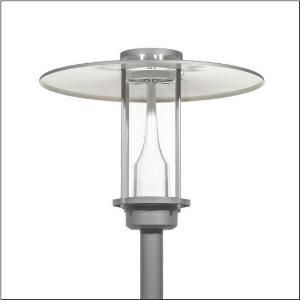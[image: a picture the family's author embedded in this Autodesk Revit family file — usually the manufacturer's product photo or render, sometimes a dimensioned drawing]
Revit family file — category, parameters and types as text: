
# Revit family: city-light_plus_iq___st1_2a_5xa5275ef14h000022_292e
name_source: partatom
category: Lighting Fixtures
units: mm (PartAtom-declared; Revit-internal decimal feet)

## family parameters
Cut with Voids When Loaded = No
Host = Face
Light Source = No
Part Type = Normal
Room Calculation Point = No
Round Connector Dimension = Use Diameter
Shared = No

## types (1)
- --- (1 x LED, 1470 lm, 10.5 W, 3000K)
    Apparent Load = 11 VA
    CIE Flux Codes = 22 62 93 97 100
    Color Rendering = 70
    Color Temperature = 3000K
    Default Elevation = 1800 mm
    Description = City-Light Plus iQ, mast luminaire, Module 540 iQ-SR, primary light control with 3 zone facetted reflector, of plastic, silver coated, highly specular, structured, primary optical cover: cover, of PMMA, transparent, light distribution: ST1.2a, light emission: direct distribution, primary light characteristic: asymmetric, installation type: post-top, LED, High Power LED, rated luminous flux: 1.470lm, luminous efficacy: 140lm/W, light colour: 730, colour temperature: 3000K, control gear: iQ Street-Remote, control: Street-Remote, Auto-Match, Temp-Guard, Lumen-Switch, Night-Set, Smart-Wire, Light-Fading, Desk-Remote (wireless, voltage-free reading and setting of iQ features in the workshop via application-optimized NFC function/RFID function), optimised constant luminous flux control (CLO 2.0), pre-setting: logarithmic dimming characteristic, mains connection: 230..240V, AC, 50/60Hz, connection cable pre-assembled, cable length: 5,5m, wiring characteristics: H07RN-F, start of lifetime: 11W, end of service life: 11W, reduction: 5W, luminaire housing, upper part, of glass-fibre reinforced polyester, coated, SITECO metallic grey (DB 702S), diameter: 750mm, height: 590mm, spigot size: d x l = 76 x 70mm (post-top) | with reducer (optional accessory) 60 x 70mm, mounting height: 3..5m, post-top mast mounting element, of diecast aluminium, coated, SITECO metallic grey (DB 702S), Module 540 iQ-SR, traffic white (RAL 9016), equipment: standard, protection rating (complete): IP65, insulation class (complete): insulation class II (safety insulation), certification: CE, ENEC, VDE, packaging unit: 1 piece

Light Distribution: ST1.2a
    Height = 590 mm
    Lamp = 1 x LED
    Lamp Light Flux = 1470 lm
    Lamp Power = 10.5 W
    Lamp count = 1
    Length = 750 mm
    Luminous efficacy = 140 lm/W
    Manufacturer = Siteco
    ModVariant = No
    Model = 5XA5275EF14H000022
    Mounting Place = Pole
    Mounting Type = Pole top
    Number of Poles = 1
    OnlyDefault = Yes
    Power Factor = 1
    Product Name = City-Light Plus iQ | ST1.2a
    Product group = mast luminaire | pylon top
    ProductGroupID = 6100
    Protection Class = Protection class II
    Protection Degree = IP 65
    RLX_Detail_Level = 1
    RLX_Emergency_Light_Flux = 0 lm
    RLX_Emergency_Type = 0
    RLX_Emergency_Type_DB = No
    RlxData = <blob elided: 51485 chars, md5=4678b270>
    Socket = socket
    Standby Power = 0 W
    System Light Flux = 1470 lm
    System Power = 11 W
    Type Comments = factory setting: luminous flux: 100 % | dim-lin: 254 | 419 mA
    Type Image = l_1006456.jpg
    URL = http://relux.com
    VarID = @adj_161085
    Voltage = 0 V
    Weight = 0.00 kg
    Width = 0 mm  [stored 0 ft]

note: [stored X ft] marks values corroborated as IEEE doubles in the binary element streams (Revit-internal decimal feet)

## geometry (parser evidence)
native form markers: Blend x4, Sweep x12
no freeform markers — native parametric forms only
